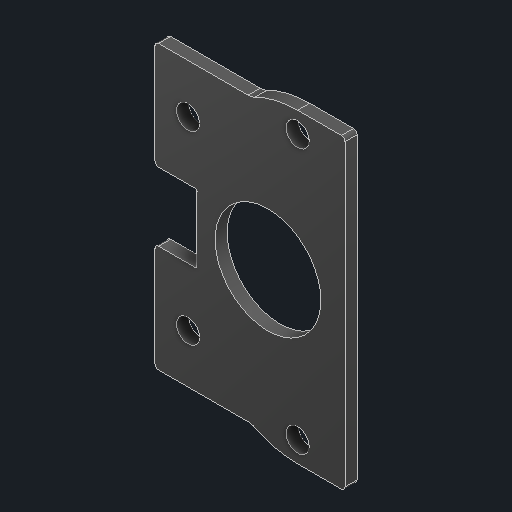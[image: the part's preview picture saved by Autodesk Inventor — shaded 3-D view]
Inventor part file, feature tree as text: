
AUTODESK INVENTOR PART (.ipt)
format: ipt  version: 2025 (Build 290162000, 162)  size: 115,200 bytes
history: native  units: in
note: dims shown in document units (in); Inventor stores cm internally (conversion verified against a paired STEP export)
features: fillet x1
ambient origin geometry x8: Origin, YZ Plane, XZ Plane, XY Plane, X Axis, Y Axis, Z Axis, Center Point
bodies: Solid1 (feature_tree)
feature tree (1):
  fillet  "Fillet1"  [1 undecoded]
note: 1 required parameter value undecoded (feature->parameter linkage not recoverable at this tier; creation-order binding heuristic only, values carry confidence <= 0.55)
